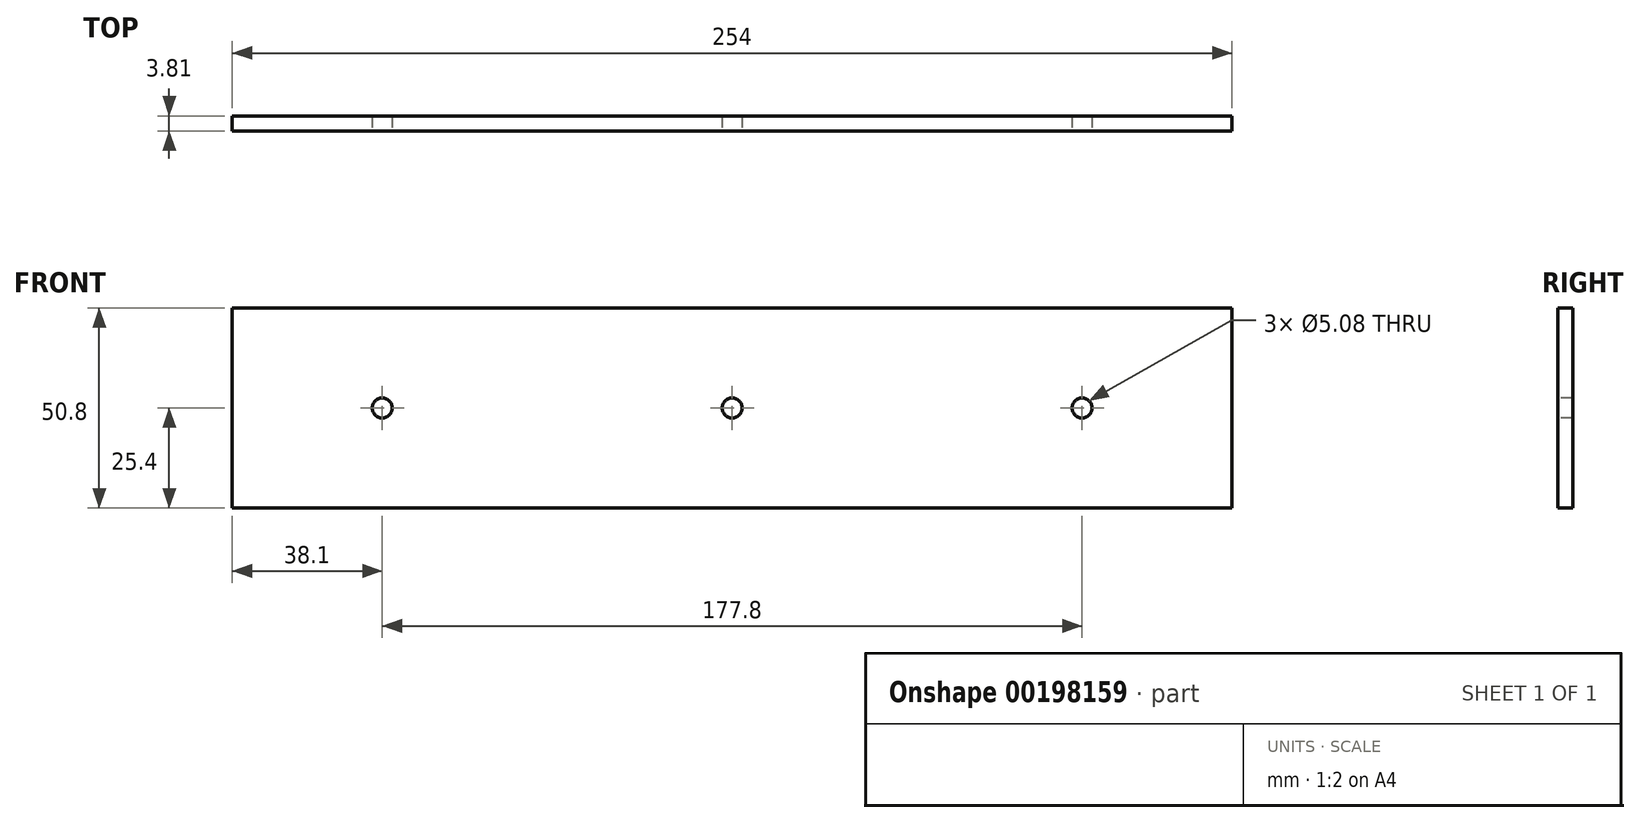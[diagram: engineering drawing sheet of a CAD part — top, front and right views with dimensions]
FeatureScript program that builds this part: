
annotation { "Feature Type Name" : "Feature", "Feature Type Description" : "" }
export const myFeature = defineFeature(function(context is Context, id is Id, definition is map)
    precondition{}
    {
        {
            var Q0;
            Q0=qCreatedBy(makeId("Front.planeOp"),FACE);
            var sketch = newSketch(context, id + "F0", { "sketchPlane" : qUnion([Q0])});
            skLineSegment(sketch, "E0.bottom", {"start": v(127, -25.4) * mm, "end": v(-127, -25.4) * mm});
            skLineSegment(sketch, "E0.top", {"start": v(127, 25.4) * mm, "end": v(-127, 25.4) * mm});
            skLineSegment(sketch, "E0.left", {"start": v(127, -25.4) * mm, "end": v(127, 25.4) * mm});
            skLineSegment(sketch, "E0.right", {"start": v(-127, -25.4) * mm, "end": v(-127, 25.4) * mm});
            skPoint(sketch, "E0.middle", {"position": v(0, 0) * mm});
            skSolve(sketch);
        }
        {
            var Q0;
            Q0 = qSketchRegion(id + "F0", true);
            extrude(context, id + "F1", {"entities" : qUnion([Q0]), "depth" : 3.8 * mm});
        }
        {
            var Q0;
            Q0=makeQuery(id+"F1.opExtrude","CAP_FACE",FACE,{"disambiguationData":[OSD([sQuery(id+"F0.wireOp",EDGE,"E0.bottom"),sQuery(id+"F0.wireOp",EDGE,"E0.top"),sQuery(id+"F0.wireOp",EDGE,"E0.left"),sQuery(id+"F0.wireOp",EDGE,"E0.right")])],"isStart":false});
            var sketch = newSketch(context, id + "F2", { "sketchPlane" : qUnion([Q0])});
            skLineSegment(sketch, "E1", {"start": v(0, 25.4) * mm, "end": v(0, 2.54) * mm});
            skLineSegment(sketch, "E2", {"start": v(-127, 0) * mm, "end": v(-91.44, 0) * mm});
            skCircle(sketch, "E3", {"center": v(-88.9, 0) * mm, "radius": 2.54 * mm});
            skLineSegment(sketch, "E4.trimOffspring", {"start": v(-86.36, 0) * mm, "end": v(-2.54, 0) * mm});
            skCircle(sketch, "E5.MirrorC", {"center": v(88.9, 0) * mm, "radius": 2.54 * mm});
            skLineSegment(sketch, "E6.trimOffspring", {"start": v(91.44, 0) * mm, "end": v(127, 0) * mm});
            skCircle(sketch, "E7", {"center": v(0, 0) * mm, "radius": 2.54 * mm});
            skLineSegment(sketch, "E8.trimOffspring", {"start": v(2.54, 0) * mm, "end": v(86.36, 0) * mm});
            skLineSegment(sketch, "E9.trimOffspring", {"start": v(0, -2.54) * mm, "end": v(0, -25.4) * mm});
            skSolve(sketch);
        }
        {
            var Q0;
            Q0 = qSketchRegion(id + "F2", true);
            extrude(context, id + "F3", {"entities" : qUnion([Q0]), "operationType" : NewBodyOperationType.REMOVE, "oppositeDirection" : true, "depth" : 25.4 * mm});
        }
    });
